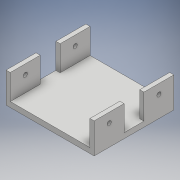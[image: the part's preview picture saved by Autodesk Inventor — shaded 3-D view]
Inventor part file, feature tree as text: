
AUTODESK INVENTOR PART (.ipt)
format: ipt  version: 2018.1 (Build 221171000, 171)  size: 159,232 bytes
history: native  units: mm
features: sketch x5, extrude x4, projected_geometry x2, other x1
ambient origin geometry x8: Origin, YZ Plane, XZ Plane, XY Plane, X Axis, Y Axis, Z Axis, Center Point
bodies: Body1 (feature_tree)
feature tree (12):
  other  "Твердое тело1"
  extrude  "Выдавливание1"  Depth=76.0mm
  extrude  "Выдавливание2"  Depth=104.76mm
  extrude  "Выдавливание3"  Depth=53.241mm
  sketch  "Эскиз4"
  extrude  "Выдавливание4"  Depth=66.1mm
  sketch  "Эскиз1"
  sketch  "Эскиз2"
  sketch  "Эскиз3"
  projected_geometry  "Спроецированная петля1"
  projected_geometry  "Спроецированная петля2"
  sketch  "Эскиз5"
